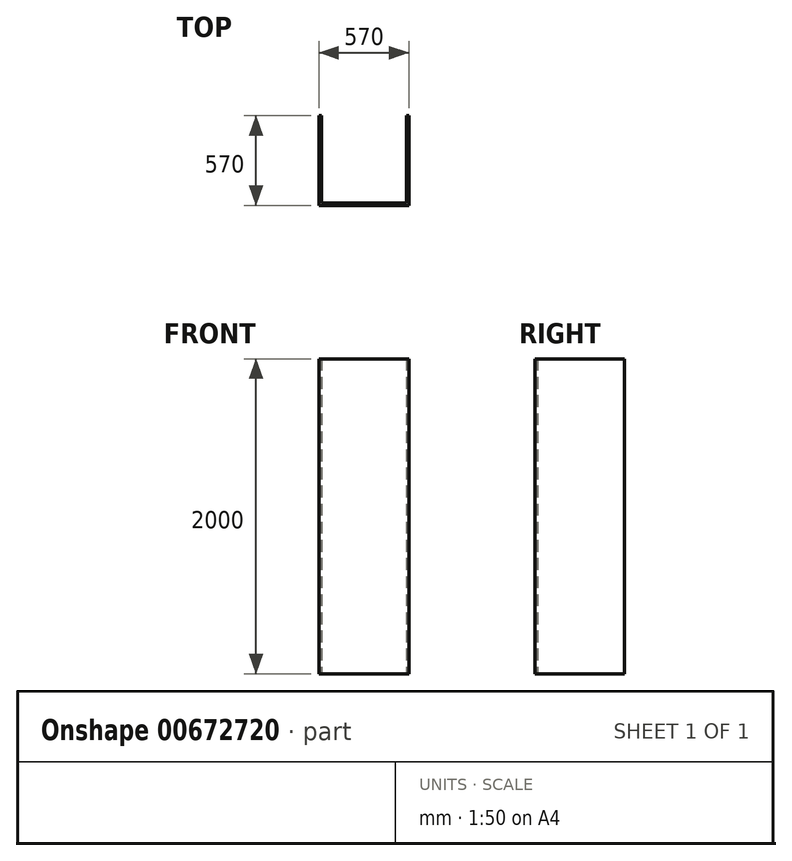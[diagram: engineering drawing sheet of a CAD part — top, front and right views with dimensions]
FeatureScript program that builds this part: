
annotation { "Feature Type Name" : "Feature", "Feature Type Description" : "" }
export const myFeature = defineFeature(function(context is Context, id is Id, definition is map)
    precondition{}
    {
        {
            var Q0;
            Q0=qCreatedBy(makeId("Top.planeOp"),FACE);
            var sketch = newSketch(context, id + "F0", { "sketchPlane" : qUnion([Q0])});
            skLineSegment(sketch, "E0.bottom", {"start": v(0, 0) * mm, "end": v(-570, 0) * mm});
            skLineSegment(sketch, "E0.top", {"start": v(0, -570) * mm, "end": v(-570, -570) * mm});
            skLineSegment(sketch, "E0.left", {"start": v(0, 0) * mm, "end": v(0, -570) * mm});
            skLineSegment(sketch, "E0.right", {"start": v(-570, 0) * mm, "end": v(-570, -570) * mm});
            skSolve(sketch);
        }
        {
            var Q0;
            Q0=makeQuery(id+"F0.imprint","IMPRINT",FACE,{"disambiguationData":[TD([[makeQuery(id+"F0.imprint","IMPRINT",EDGE,{"derivedFrom":sQuery(id+"F0.wireOp",EDGE,"Y66rWitT-qBWe-ztKi-yuPp-pPcdfemAuZkT.bottom")}),-1.0]])]});
            var Q1;
            Q1=makeQuery(id+"F0.imprint","IMPRINT",FACE,{"disambiguationData":[TD([[makeQuery(id+"F0.imprint","IMPRINT",EDGE,{"derivedFrom":sQuery(id+"F0.wireOp",EDGE,"E0.bottom")}),1.0]])]});
            extrude(context, id + "F1", {"entities" : qUnion([Q0, Q1]), "depth" : 2000 * mm, "offsetDistance" : 25 * mm});
        }
        {
            var Q0;
            Q0=makeQuery(id+"F1.opExtrude","SWEPT_FACE",FACE,{"disambiguationData":[OSD([sQuery(id+"F0.wireOp",EDGE,"E0.bottom")])]});
            var Q1;
            Q1=makeQuery(id+"F1.opExtrude","CAP_FACE",FACE,{"disambiguationData":[OSD([sQuery(id+"F0.wireOp",EDGE,"E0.bottom"),sQuery(id+"F0.wireOp",EDGE,"E0.top"),sQuery(id+"F0.wireOp",EDGE,"E0.left"),sQuery(id+"F0.wireOp",EDGE,"E0.right")])],"isStart":false});
            var Q2;
            Q2=makeQuery(id+"F1.opExtrude","CAP_FACE",FACE,{"disambiguationData":[OSD([sQuery(id+"F0.wireOp",EDGE,"E0.bottom"),sQuery(id+"F0.wireOp",EDGE,"E0.top"),sQuery(id+"F0.wireOp",EDGE,"E0.left"),sQuery(id+"F0.wireOp",EDGE,"E0.right")])],"isStart":true});
            shell(context, id + "F2", {"entities" : qUnion([Q0, Q1, Q2]), "thickness" : 16 * mm});
        }
    });
